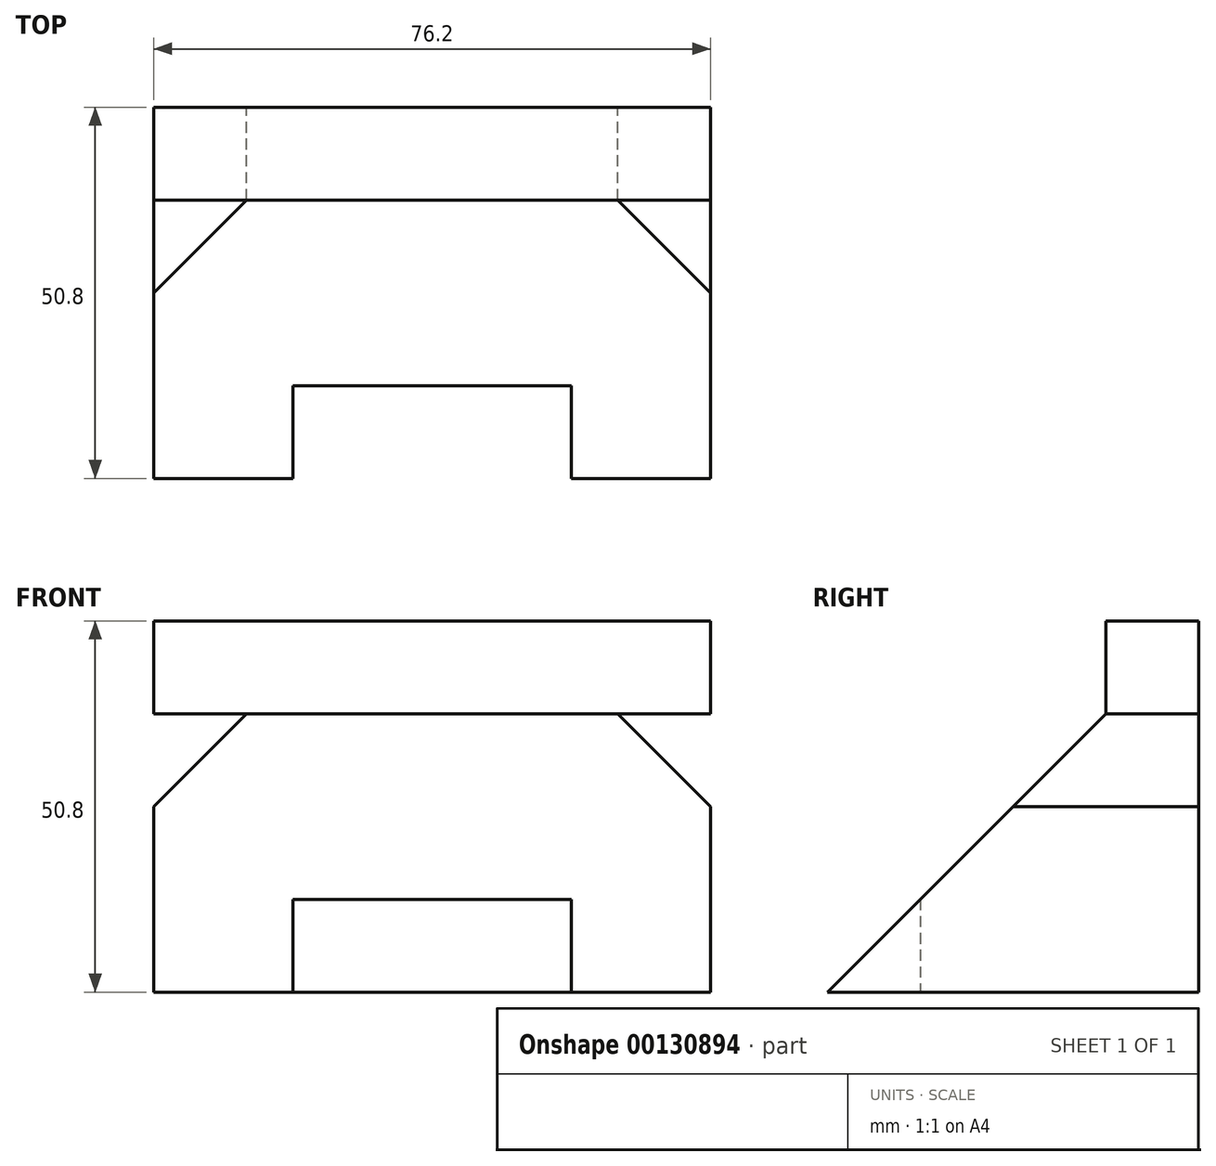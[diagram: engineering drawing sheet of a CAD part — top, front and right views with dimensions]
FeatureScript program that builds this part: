
annotation { "Feature Type Name" : "Feature", "Feature Type Description" : "" }
export const myFeature = defineFeature(function(context is Context, id is Id, definition is map)
    precondition{}
    {
        {
            var Q0;
            Q0=qCreatedBy(makeId("Right.planeOp"),FACE);
            var sketch = newSketch(context, id + "F0", { "sketchPlane" : qUnion([Q0])});
            skLineSegment(sketch, "E0", {"start": v(0, 0) * mm, "end": v(38.1, 0) * mm});
            skLineSegment(sketch, "E1", {"start": v(38.1, 0) * mm, "end": v(38.1, 38.1) * mm});
            skLineSegment(sketch, "E2", {"start": v(38.1, 38.1) * mm, "end": v(0, 0) * mm});
            skLineSegment(sketch, "E3.bottom", {"start": v(38.1, 0) * mm, "end": v(50.8, 0) * mm});
            skLineSegment(sketch, "E3.top", {"start": v(38.1, 50.8) * mm, "end": v(50.8, 50.8) * mm});
            skLineSegment(sketch, "E3.left", {"start": v(38.1, 0) * mm, "end": v(38.1, 50.8) * mm});
            skLineSegment(sketch, "E3.right", {"start": v(50.8, 0) * mm, "end": v(50.8, 50.8) * mm});
            skLineSegment(sketch, "E4", {"start": v(38.1, 25.4) * mm, "end": v(38.1, 0) * mm});
            skLineSegment(sketch, "E5", {"start": v(38.1, 25.4) * mm, "end": v(50.8, 25.4) * mm});
            skLineSegment(sketch, "E6", {"start": v(50.8, 25.4) * mm, "end": v(50.8, 0) * mm});
            skSolve(sketch);
        }
        {
            var Q0;
            Q0=qSketchRegion(id+"F0",true);
            extrude(context, id + "F1", {"entities" : qUnion([Q0]), "depth" : 76.2 * mm});
        }
        {
            var Q0;
            Q0=makeQuery(id+"F1.opExtrude","SWEPT_FACE",FACE,{"disambiguationData":[OSD([sQuery(id+"F0.wireOp",EDGE,"E0"),sQuery(id+"F0.wireOp",EDGE,"E3.bottom")])]});
            var sketch = newSketch(context, id + "F2", { "sketchPlane" : qUnion([Q0])});
            skLineSegment(sketch, "E7", {"start": v(19.05, 0) * mm, "end": v(57.15, 0) * mm});
            skLineSegment(sketch, "E8", {"start": v(57.15, 0) * mm, "end": v(57.15, -12.7) * mm});
            skLineSegment(sketch, "E9", {"start": v(57.15, -12.7) * mm, "end": v(19.05, -12.7) * mm});
            skLineSegment(sketch, "E10", {"start": v(19.05, -12.7) * mm, "end": v(19.05, 0) * mm});
            skLineSegment(sketch, "E11.0", {"start": v(0, 0) * mm, "end": v(0, -50.8) * mm});
            skLineSegment(sketch, "E12.0", {"start": v(76.2, -50.8) * mm, "end": v(0, -50.8) * mm});
            skLineSegment(sketch, "E13.0", {"start": v(76.2, 0) * mm, "end": v(76.2, -50.8) * mm});
            skLineSegment(sketch, "E14", {"start": v(0, 0) * mm, "end": v(19.05, 0) * mm});
            skLineSegment(sketch, "E15", {"start": v(57.15, 0) * mm, "end": v(76.2, 0) * mm});
            skSolve(sketch);
        }
        {
            var Q0;
            Q0=makeQuery(id+"F2.imprint","IMPRINT",FACE,{"disambiguationData":[TD([[makeQuery(id+"F2.imprint","IMPRINT",EDGE,{"derivedFrom":sQuery(id+"F2.wireOp",EDGE,"E8")}),-1.0]])]});
            extrude(context, id + "F3", {"entities" : qUnion([Q0]), "operationType" : NewBodyOperationType.REMOVE, "endBound" : BoundingType.THROUGH_ALL, "oppositeDirection" : true, "depth" : 25.4 * mm});
        }
        {
            var Q0;
            Q0=makeQuery(id+"F1.opExtrude","SWEPT_FACE",FACE,{"disambiguationData":[OSD([sQuery(id+"F0.wireOp",EDGE,"E3.right"),sQuery(id+"F0.wireOp",EDGE,"E6")])]});
            var sketch = newSketch(context, id + "F4", { "sketchPlane" : qUnion([Q0])});
            skLineSegment(sketch, "E16.top", {"start": v(-76.2, 38.1) * mm, "end": v(0, 38.1) * mm});
            skLineSegment(sketch, "E16.left", {"start": v(-76.2, 50.8) * mm, "end": v(-76.2, 38.1) * mm});
            skLineSegment(sketch, "E16.right", {"start": v(0, 50.8) * mm, "end": v(0, 38.1) * mm});
            skLineSegment(sketch, "E17", {"start": v(-76.2, 50.8) * mm, "end": v(0, 50.8) * mm});
            skLineSegment(sketch, "E18", {"start": v(0, 38.1) * mm, "end": v(0, 0) * mm});
            skLineSegment(sketch, "E19", {"start": v(0, 0) * mm, "end": v(-76.2, 0) * mm});
            skLineSegment(sketch, "E20", {"start": v(-76.2, 0) * mm, "end": v(-76.2, 38.1) * mm});
            skLineSegment(sketch, "E21", {"start": v(-50.8, 50.8) * mm, "end": v(-50.8, 38.1) * mm});
            skLineSegment(sketch, "E22", {"start": v(-25.4, 50.8) * mm, "end": v(-25.4, 38.1) * mm});
            skLineSegment(sketch, "E23", {"start": v(-50.8, 50.8) * mm, "end": v(-76.2, 25.4) * mm});
            skLineSegment(sketch, "E24", {"start": v(-25.4, 50.8) * mm, "end": v(0, 25.4) * mm});
            skSolve(sketch);
        }
        {
            var Q0;
            {var subQ0=sQuery(id+"F4.wireOp",EDGE,"E16.left");Q0=makeQuery(id+"F4.imprint","IMPRINT",FACE,{"disambiguationData":[TD([[makeQuery(id+"F4.imprint","IMPRINT",EDGE,{"derivedFrom":subQ0}),1.0]])]});}
            var Q1;
            {var subQ0=sQuery(id+"F4.wireOp",EDGE,"E16.right");Q1=makeQuery(id+"F4.imprint","IMPRINT",FACE,{"disambiguationData":[TD([[makeQuery(id+"F4.imprint","IMPRINT",EDGE,{"derivedFrom":subQ0}),-1.0]])]});}
            var Q2;
            {var subQ0=sQuery(id+"F4.wireOp",EDGE,"E18");var subQ3=sQuery(id+"F4.wireOp",EDGE,"E24");var subQ5=makeQuery(id+"F4.imprint","INTERSECT",VERTEX,{"derivedFrom":[subQ0,subQ3]});Q2=makeQuery(id+"F4.imprint","IMPRINT",FACE,{"disambiguationData":[TD([[makeQuery(id+"F4.imprint","IMPRINT",EDGE,{"disambiguationData":[TD([[subQ5,1.0]])],"derivedFrom":subQ3}),1.0]])]});}
            var Q3;
            {var subQ0=sQuery(id+"F4.wireOp",EDGE,"E20");var subQ3=sQuery(id+"F4.wireOp",EDGE,"E23");var subQ5=makeQuery(id+"F4.imprint","INTERSECT",VERTEX,{"derivedFrom":[subQ0,subQ3]});Q3=makeQuery(id+"F4.imprint","IMPRINT",FACE,{"disambiguationData":[TD([[makeQuery(id+"F4.imprint","IMPRINT",EDGE,{"disambiguationData":[TD([[subQ5,1.0]])],"derivedFrom":subQ3}),-1.0]])]});}
            extrude(context, id + "F5", {"entities" : qUnion([Q0, Q1, Q2, Q3]), "operationType" : NewBodyOperationType.REMOVE, "endBound" : BoundingType.THROUGH_ALL, "oppositeDirection" : true, "depth" : 25.4 * mm});
        }
    });
